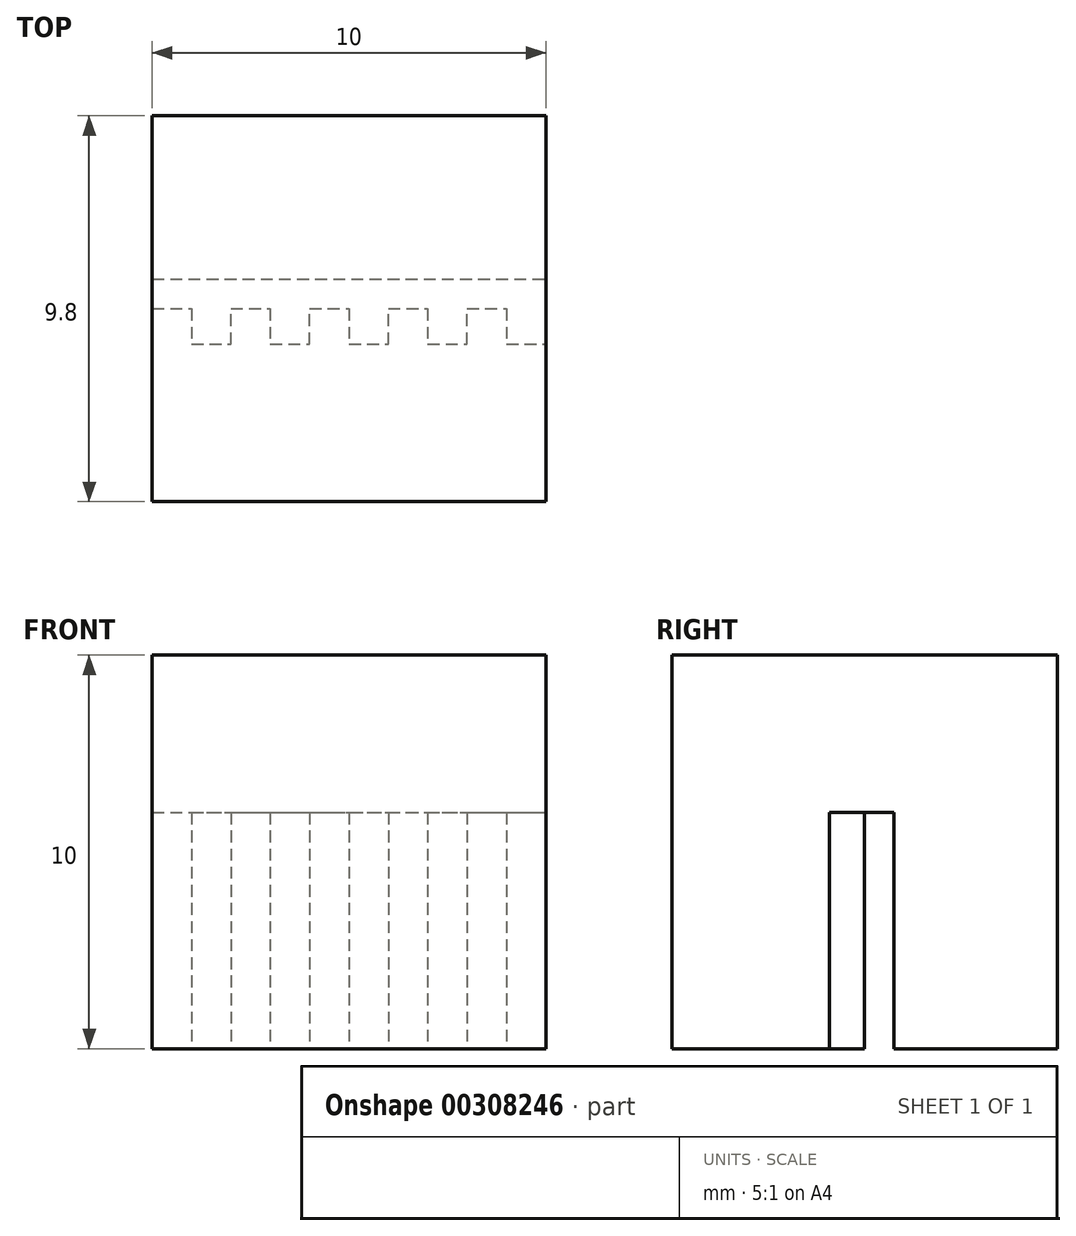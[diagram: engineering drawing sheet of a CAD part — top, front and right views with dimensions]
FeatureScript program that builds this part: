
annotation { "Feature Type Name" : "Feature", "Feature Type Description" : "" }
export const myFeature = defineFeature(function(context is Context, id is Id, definition is map)
    precondition{}
    {
        {
            var Q0;
            Q0=qCreatedBy(makeId("Top.planeOp"),FACE);
            var sketch = newSketch(context, id + "F0", { "sketchPlane" : qUnion([Q0])});
            skLineSegment(sketch, "E0.bottom", {"start": v(-5, 5.8) * mm, "end": v(5, 5.8) * mm});
            skLineSegment(sketch, "E0.top", {"start": v(-5, -4) * mm, "end": v(5, -4) * mm});
            skLineSegment(sketch, "E0.left", {"start": v(-5, 5.8) * mm, "end": v(-5, -4) * mm});
            skLineSegment(sketch, "E0.right", {"start": v(5, 5.8) * mm, "end": v(5, -4) * mm});
            skLineSegment(sketch, "E1", {"start": v(-5, 1.65) * mm, "end": v(5, 1.65) * mm});
            skLineSegment(sketch, "E2", {"start": v(-5, 0.9) * mm, "end": v(-4, 0.9) * mm});
            skLineSegment(sketch, "E3", {"start": v(-4, 0.9) * mm, "end": v(-4, 0) * mm});
            skLineSegment(sketch, "E4", {"start": v(-4, 0) * mm, "end": v(-3, 0) * mm});
            skLineSegment(sketch, "E5", {"start": v(-3, 0) * mm, "end": v(-3, 0.9) * mm});
            skLineSegment(sketch, "E6", {"start": v(-3, 0.9) * mm, "end": v(-2, 0.9) * mm});
            skLineSegment(sketch, "E7", {"start": v(-2, 0.9) * mm, "end": v(-2, 0) * mm});
            skLineSegment(sketch, "E8", {"start": v(-2, 0) * mm, "end": v(-1, 0) * mm});
            skLineSegment(sketch, "E9", {"start": v(-1, 0) * mm, "end": v(-1, 0.9) * mm});
            skLineSegment(sketch, "E10", {"start": v(-1, 0.9) * mm, "end": v(0, 0.9) * mm});
            skLineSegment(sketch, "E11", {"start": v(0, 0.9) * mm, "end": v(0, 0) * mm});
            skLineSegment(sketch, "E12", {"start": v(0, 0) * mm, "end": v(1, 0) * mm});
            skLineSegment(sketch, "E13", {"start": v(1, 0) * mm, "end": v(1, 0.9) * mm});
            skLineSegment(sketch, "E14", {"start": v(1, 0.9) * mm, "end": v(2, 0.9) * mm});
            skLineSegment(sketch, "E15", {"start": v(2, 0.9) * mm, "end": v(2, 0) * mm});
            skLineSegment(sketch, "E16", {"start": v(2, 0) * mm, "end": v(3, 0) * mm});
            skLineSegment(sketch, "E17", {"start": v(3, 0) * mm, "end": v(3, 0.9) * mm});
            skLineSegment(sketch, "E18", {"start": v(3, 0.9) * mm, "end": v(4, 0.9) * mm});
            skLineSegment(sketch, "E19", {"start": v(4, 0.9) * mm, "end": v(4, 0) * mm});
            skLineSegment(sketch, "E20", {"start": v(4, 0) * mm, "end": v(5, 0) * mm});
            skSolve(sketch);
        }
        {
            var Q0;
            {var subQ0=sQuery(id+"F0.wireOp",EDGE,"E0.bottom");Q0=makeQuery(id+"F0.imprint","IMPRINT",FACE,{"disambiguationData":[TD([[makeQuery(id+"F0.imprint","IMPRINT",EDGE,{"derivedFrom":subQ0}),-1.0]])]});}
            var Q1;
            {var subQ0=sQuery(id+"F0.wireOp",EDGE,"E1");Q1=makeQuery(id+"F0.imprint","IMPRINT",FACE,{"disambiguationData":[TD([[makeQuery(id+"F0.imprint","IMPRINT",EDGE,{"derivedFrom":subQ0}),-1.0]])]});}
            var Q2;
            {var subQ0=sQuery(id+"F0.wireOp",EDGE,"E0.top");Q2=makeQuery(id+"F0.imprint","IMPRINT",FACE,{"disambiguationData":[TD([[makeQuery(id+"F0.imprint","IMPRINT",EDGE,{"derivedFrom":subQ0}),1.0]])]});}
            extrude(context, id + "F1", {"entities" : qUnion([Q0, Q1, Q2]), "depth" : 10 * mm});
        }
        {
            var Q0;
            {var subQ0=sQuery(id+"F0.wireOp",EDGE,"E1");Q0=makeQuery(id+"F0.imprint","IMPRINT",FACE,{"disambiguationData":[TD([[makeQuery(id+"F0.imprint","IMPRINT",EDGE,{"derivedFrom":subQ0}),-1.0]])]});}
            extrude(context, id + "F2", {"entities" : qUnion([Q0]), "operationType" : NewBodyOperationType.REMOVE, "depth" : 6 * mm});
        }
    });
